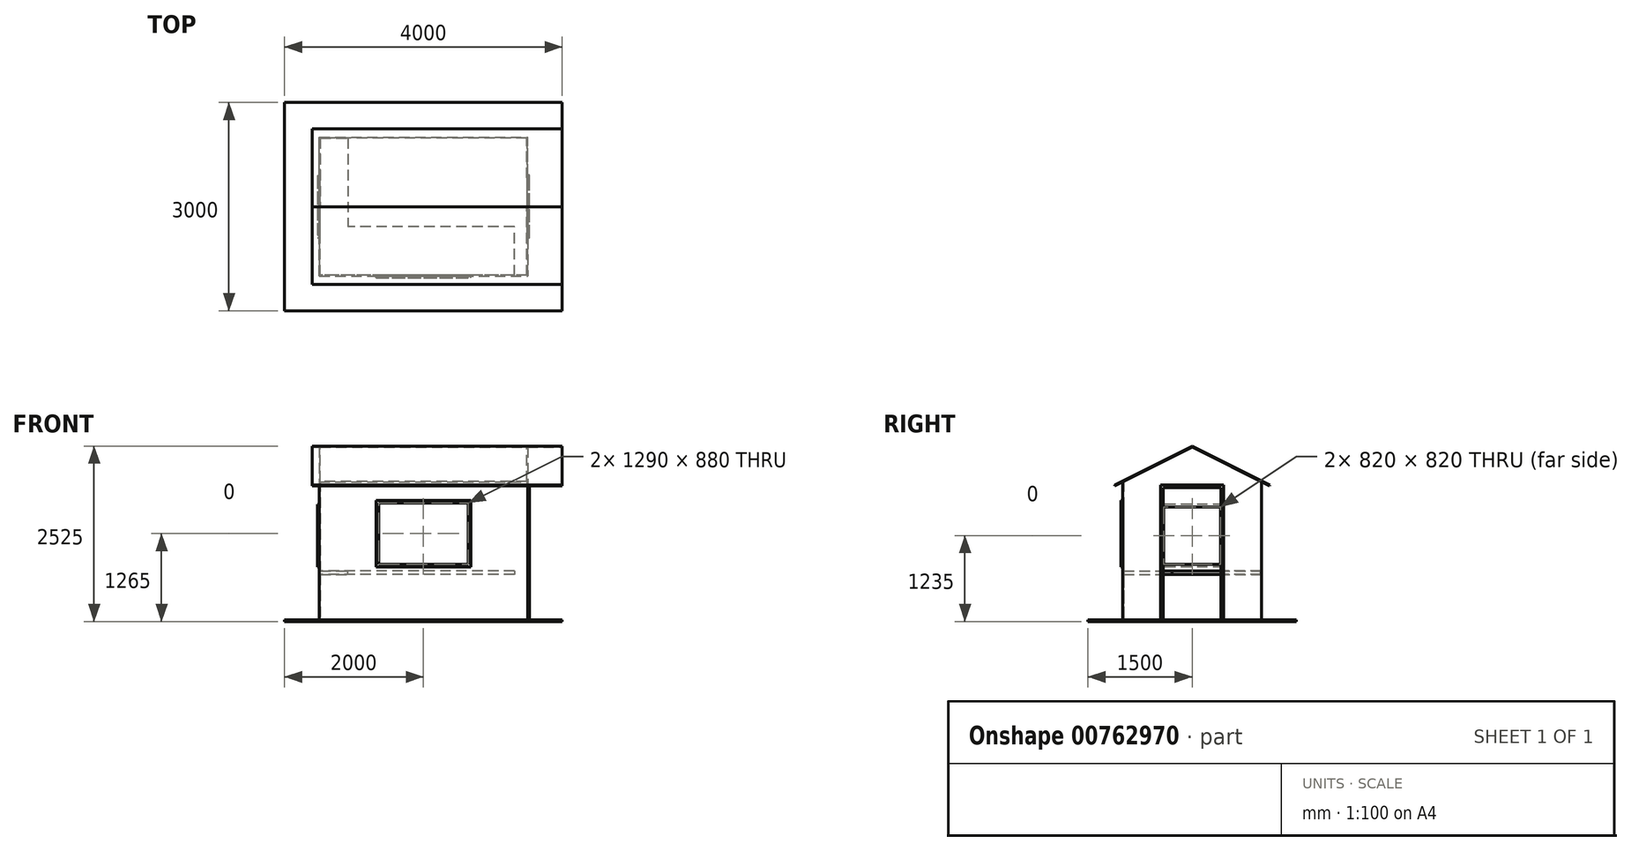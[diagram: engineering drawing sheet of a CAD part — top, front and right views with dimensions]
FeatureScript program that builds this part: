
annotation { "Feature Type Name" : "Feature", "Feature Type Description" : "" }
export const myFeature = defineFeature(function(context is Context, id is Id, definition is map)
    precondition{}
    {
        {
            var Q0;
            Q0=qCreatedBy(makeId("Top.planeOp"),FACE);
            var sketch = newSketch(context, id + "F0", { "sketchPlane" : qUnion([Q0])});
            skLineSegment(sketch, "E0.bottom", {"start": v(2000, 1500) * mm, "end": v(-2000, 1500) * mm});
            skLineSegment(sketch, "E0.top", {"start": v(2000, -1500) * mm, "end": v(-2000, -1500) * mm});
            skLineSegment(sketch, "E0.left", {"start": v(2000, 1500) * mm, "end": v(2000, -1500) * mm});
            skLineSegment(sketch, "E0.right", {"start": v(-2000, 1500) * mm, "end": v(-2000, -1500) * mm});
            skPoint(sketch, "E0.middle", {"position": v(0, 0) * mm});
            skSolve(sketch);
        }
        {
            var Q0;
            Q0 = qSketchRegion(id + "F0", true);
            extrude(context, id + "F1", {"entities" : qUnion([Q0]), "depth" : 25 * mm, "offsetDistance" : 25 * mm});
        }
        {
            var Q0;
            Q0=makeQuery(id+"F1.opExtrude","CAP_FACE",FACE,{"disambiguationData":[OSD([sQuery(id+"F0.wireOp",EDGE,"E0.bottom"),sQuery(id+"F0.wireOp",EDGE,"E0.top"),sQuery(id+"F0.wireOp",EDGE,"E0.left"),sQuery(id+"F0.wireOp",EDGE,"E0.right")])],"isStart":false});
            var sketch = newSketch(context, id + "F2", { "sketchPlane" : qUnion([Q0])});
            skLineSegment(sketch, "E1.bottom", {"start": v(1500, -1000) * mm, "end": v(-1500, -1000) * mm});
            skLineSegment(sketch, "E1.top", {"start": v(1500, 1000) * mm, "end": v(-1500, 1000) * mm});
            skLineSegment(sketch, "E1.left", {"start": v(1500, -1000) * mm, "end": v(1500, 1000) * mm});
            skLineSegment(sketch, "E1.right", {"start": v(-1500, -1000) * mm, "end": v(-1500, 1000) * mm});
            skPoint(sketch, "E1.middle", {"position": v(0, 0) * mm});
            skLineSegment(sketch, "E2.0", {"start": v(-1488, -988) * mm, "end": v(-1488, 988) * mm});
            skLineSegment(sketch, "E2.1", {"start": v(1488, -988) * mm, "end": v(-1488, -988) * mm});
            skLineSegment(sketch, "E2.2", {"start": v(1488, -988) * mm, "end": v(1488, 988) * mm});
            skLineSegment(sketch, "E2.3", {"start": v(1488, 988) * mm, "end": v(-1488, 988) * mm});
            skSolve(sketch);
        }
        {
            var Q0;
            Q0 = qSketchRegion(id + "F2", true);
            extrude(context, id + "F3", {"entities" : qUnion([Q0]), "depth" : 2500 * mm, "offsetDistance" : 25 * mm});
        }
        {
            var Q0;
            Q0=makeQuery(id+"F3.opExtrude","SWEPT_FACE",FACE,{"disambiguationData":[OSD([sQuery(id+"F2.wireOp",EDGE,"E1.right")])]});
            var sketch = newSketch(context, id + "F4", { "sketchPlane" : qUnion([Q0])});
            skLineSegment(sketch, "E3.bottom", {"start": v(-410, 1645) * mm, "end": v(410, 1645) * mm});
            skLineSegment(sketch, "E3.top", {"start": v(-410, 825) * mm, "end": v(410, 825) * mm});
            skLineSegment(sketch, "E3.left", {"start": v(-410, 1645) * mm, "end": v(-410, 825) * mm});
            skLineSegment(sketch, "E3.right", {"start": v(410, 1645) * mm, "end": v(410, 825) * mm});
            skLineSegment(sketch, "E4", {"start": v(0, 2525) * mm, "end": v(0, 25) * mm, "construction": true});
            skLineSegment(sketch, "E5.0", {"start": v(-450, 1685) * mm, "end": v(-450, 785) * mm});
            skLineSegment(sketch, "E5.1", {"start": v(-450, 1685) * mm, "end": v(450, 1685) * mm});
            skLineSegment(sketch, "E5.2", {"start": v(450, 1685) * mm, "end": v(450, 785) * mm});
            skLineSegment(sketch, "E5.3", {"start": v(-450, 785) * mm, "end": v(450, 785) * mm});
            skSolve(sketch);
        }
        {
            var Q0;
            Q0 = qSketchRegion(id + "F4", true);
            extrude(context, id + "F5", {"entities" : qUnion([Q0]), "depth" : 25 * mm, "offsetDistance" : 25 * mm});
        }
        {
            var Q0;
            Q0=makeQuery(id+"F4.imprint","IMPRINT",FACE,{"disambiguationData":[TD([[makeQuery(id+"F4.imprint","IMPRINT",EDGE,{"derivedFrom":sQuery(id+"F4.wireOp",EDGE,"E3.bottom")}),-1.0]])]});
            var Q1;
            Q1=makeQuery(id+"F3.opExtrude","SWEPT_FACE",FACE,{"disambiguationData":[OSD([sQuery(id+"F2.wireOp",EDGE,"E2.0")])]});
            extrude(context, id + "F6", {"entities" : qUnion([Q0]), "operationType" : NewBodyOperationType.REMOVE, "endBound" : BoundingType.UP_TO_SURFACE, "oppositeDirection" : true, "depth" : 25 * mm, "endBoundEntityFace" : qUnion([Q1]), "offsetDistance" : 25 * mm});
        }
        {
            var Q0;
            Q0=makeQuery(id+"F3.opExtrude","SWEPT_FACE",FACE,{"disambiguationData":[OSD([sQuery(id+"F2.wireOp",EDGE,"E1.bottom")])]});
            var sketch = newSketch(context, id + "F7", { "sketchPlane" : qUnion([Q0])});
            skLineSegment(sketch, "E6.bottom", {"start": v(-645, 825) * mm, "end": v(645, 825) * mm});
            skLineSegment(sketch, "E6.top", {"start": v(-645, 1705) * mm, "end": v(645, 1705) * mm});
            skLineSegment(sketch, "E6.left", {"start": v(-645, 825) * mm, "end": v(-645, 1705) * mm});
            skLineSegment(sketch, "E6.right", {"start": v(645, 825) * mm, "end": v(645, 1705) * mm});
            skLineSegment(sketch, "E7.0", {"start": v(-685, 1745) * mm, "end": v(685, 1745) * mm});
            skLineSegment(sketch, "E7.1", {"start": v(-685, 785) * mm, "end": v(-685, 1745) * mm});
            skLineSegment(sketch, "E7.2", {"start": v(-685, 785) * mm, "end": v(685, 785) * mm});
            skLineSegment(sketch, "E7.3", {"start": v(685, 785) * mm, "end": v(685, 1745) * mm});
            skLineSegment(sketch, "E8", {"start": v(0, 2525) * mm, "end": v(0, 25) * mm, "construction": true});
            skSolve(sketch);
        }
        {
            var Q0;
            Q0 = qSketchRegion(id + "F7", true);
            extrude(context, id + "F8", {"entities" : qUnion([Q0]), "depth" : 25 * mm, "offsetDistance" : 25 * mm});
        }
        {
            var Q0;
            Q0=makeQuery(id+"F7.imprint","IMPRINT",FACE,{"disambiguationData":[TD([[makeQuery(id+"F7.imprint","IMPRINT",EDGE,{"derivedFrom":sQuery(id+"F7.wireOp",EDGE,"E6.bottom")}),1.0]])]});
            var Q1;
            Q1=makeQuery(id+"F3.opExtrude","SWEPT_FACE",FACE,{"disambiguationData":[OSD([sQuery(id+"F2.wireOp",EDGE,"E2.1")])]});
            extrude(context, id + "F9", {"entities" : qUnion([Q0]), "operationType" : NewBodyOperationType.REMOVE, "endBound" : BoundingType.UP_TO_SURFACE, "oppositeDirection" : true, "depth" : 25 * mm, "endBoundEntityFace" : qUnion([Q1]), "offsetDistance" : 25 * mm});
        }
        {
            var Q0;
            Q0=makeQuery(id+"F3.opExtrude","SWEPT_FACE",FACE,{"disambiguationData":[OSD([sQuery(id+"F2.wireOp",EDGE,"E1.left")])]});
            var sketch = newSketch(context, id + "F10", { "sketchPlane" : qUnion([Q0])});
            skLineSegment(sketch, "E9.bottom", {"start": v(-415, 25) * mm, "end": v(415, 25) * mm});
            skLineSegment(sketch, "E9.top", {"start": v(-415, 1925) * mm, "end": v(415, 1925) * mm});
            skLineSegment(sketch, "E9.left", {"start": v(-415, 25) * mm, "end": v(-415, 1925) * mm});
            skLineSegment(sketch, "E9.right", {"start": v(415, 25) * mm, "end": v(415, 1925) * mm});
            skLineSegment(sketch, "E10", {"start": v(0, 2525) * mm, "end": v(0, 0) * mm, "construction": true});
            skLineSegment(sketch, "E11.0", {"start": v(-455, 25) * mm, "end": v(-455, 1965) * mm});
            skLineSegment(sketch, "E11.1", {"start": v(-455, 1965) * mm, "end": v(455, 1965) * mm});
            skLineSegment(sketch, "E11.2", {"start": v(455, 25) * mm, "end": v(455, 1965) * mm});
            skLineSegment(sketch, "E12", {"start": v(0, 2525) * mm, "end": v(1000, 2025) * mm});
            skLineSegment(sketch, "E13", {"start": v(0, 2525) * mm, "end": v(-1000, 2025) * mm});
            skLineSegment(sketch, "E14.0", {"start": v(0, 2511.58) * mm, "end": v(-1000, 2011.58) * mm});
            skLineSegment(sketch, "E14.1", {"start": v(0, 2511.58) * mm, "end": v(1000, 2011.58) * mm});
            skLineSegment(sketch, "E15", {"start": v(-1000, 2025) * mm, "end": v(-1118.03, 1965.98) * mm});
            skLineSegment(sketch, "E16", {"start": v(-1118.03, 1965.98) * mm, "end": v(-1112.67, 1955.25) * mm});
            skLineSegment(sketch, "E17", {"start": v(-1112.67, 1955.25) * mm, "end": v(-1000, 2011.58) * mm});
            skLineSegment(sketch, "E18.MirrorCS", {"start": v(1118.03, 1965.98) * mm, "end": v(1112.67, 1955.25) * mm});
            skLineSegment(sketch, "E19.MirrorCS", {"start": v(1000, 2025) * mm, "end": v(1118.03, 1965.98) * mm});
            skLineSegment(sketch, "E20.MirrorCS", {"start": v(1112.67, 1955.25) * mm, "end": v(1000, 2011.58) * mm});
            skSolve(sketch);
        }
        {
            var Q0;
            Q0=makeQuery(id+"F10.imprint","IMPRINT",FACE,{"disambiguationData":[TD([[makeQuery(id+"F10.imprint","IMPRINT",EDGE,{"derivedFrom":sQuery(id+"F10.wireOp",EDGE,"E9.top")}),1.0]])]});
            extrude(context, id + "F11", {"entities" : qUnion([Q0]), "depth" : 25 * mm, "offsetDistance" : 25 * mm});
        }
        {
            var Q0;
            Q0=makeQuery(id+"F10.imprint","IMPRINT",FACE,{"disambiguationData":[TD([[makeQuery(id+"F10.imprint","IMPRINT",EDGE,{"derivedFrom":sQuery(id+"F10.wireOp",EDGE,"E9.bottom")}),1.0]])]});
            extrude(context, id + "F12", {"entities" : qUnion([Q0]), "operationType" : NewBodyOperationType.REMOVE, "oppositeDirection" : true, "depth" : 25 * mm, "offsetDistance" : 25 * mm});
        }
        {
            var Q0;
            {var subQ0=sQuery(id+"F10.wireOp",EDGE,"E13");Q0=makeQuery(id+"F10.imprint","IMPRINT",FACE,{"disambiguationData":[TD([[makeQuery(id+"F10.imprint","IMPRINT",EDGE,{"derivedFrom":subQ0}),-1.0]])]});}
            var Q1;
            {var subQ0=sQuery(id+"F10.wireOp",EDGE,"E12");Q1=makeQuery(id+"F10.imprint","IMPRINT",FACE,{"disambiguationData":[TD([[makeQuery(id+"F10.imprint","IMPRINT",EDGE,{"derivedFrom":subQ0}),1.0]])]});}
            var Q2;
            {var subQ5=sQuery(id+"F10.wireOp",EDGE,"E12");Q2=makeQuery(id+"F10.imprint","IMPRINT",FACE,{"disambiguationData":[TD([[makeQuery(id+"F10.imprint","IMPRINT",EDGE,{"derivedFrom":subQ5}),-1.0]])]});}
            var Q3;
            Q3=makeQuery(id+"F3.opExtrude","SWEPT_FACE",FACE,{"disambiguationData":[OSD([sQuery(id+"F2.wireOp",EDGE,"E1.right")])]});
            extrude(context, id + "F13", {"entities" : qUnion([Q0, Q1, Q2]), "operationType" : NewBodyOperationType.REMOVE, "endBound" : BoundingType.UP_TO_SURFACE, "oppositeDirection" : true, "depth" : 25 * mm, "endBoundEntityFace" : qUnion([Q3]), "offsetDistance" : 25 * mm});
        }
        {
            var Q0;
            {var subQ5=sQuery(id+"F10.wireOp",EDGE,"E12");Q0=makeQuery(id+"F10.imprint","IMPRINT",FACE,{"disambiguationData":[TD([[makeQuery(id+"F10.imprint","IMPRINT",EDGE,{"derivedFrom":subQ5}),-1.0]])]});}
            var Q1;
            Q1=makeQuery(id+"F10.imprint","IMPRINT",FACE,{"disambiguationData":[TD([[makeQuery(id+"F10.imprint","IMPRINT",EDGE,{"derivedFrom":sQuery(id+"F10.wireOp",EDGE,"E18.MirrorCS")}),-1.0]])]});
            var Q2;
            {var subQ0=sQuery(id+"F10.wireOp",EDGE,"E15");Q2=makeQuery(id+"F10.imprint","IMPRINT",FACE,{"disambiguationData":[TD([[makeQuery(id+"F10.imprint","IMPRINT",EDGE,{"derivedFrom":subQ0}),1.0]])]});}
            extrude(context, id + "F14", {"entities" : qUnion([Q0, Q1, Q2]), "oppositeDirection" : true, "depth" : 3100 * mm, "offsetDistance" : 25 * mm});
        }
        {
            var Q0;
            {var subQ0=sQuery(id+"F10.wireOp",EDGE,"E15");Q0=makeQuery(id+"F10.imprint","IMPRINT",FACE,{"disambiguationData":[TD([[makeQuery(id+"F10.imprint","IMPRINT",EDGE,{"derivedFrom":subQ0}),1.0]])]});}
            var Q1;
            {var subQ5=sQuery(id+"F10.wireOp",EDGE,"E12");Q1=makeQuery(id+"F10.imprint","IMPRINT",FACE,{"disambiguationData":[TD([[makeQuery(id+"F10.imprint","IMPRINT",EDGE,{"derivedFrom":subQ5}),-1.0]])]});}
            var Q2;
            Q2=makeQuery(id+"F10.imprint","IMPRINT",FACE,{"disambiguationData":[TD([[makeQuery(id+"F10.imprint","IMPRINT",EDGE,{"derivedFrom":sQuery(id+"F10.wireOp",EDGE,"E18.MirrorCS")}),-1.0]])]});
            extrude(context, id + "F15", {"entities" : qUnion([Q0, Q1, Q2]), "operationType" : NewBodyOperationType.ADD, "depth" : 500 * mm, "offsetDistance" : 25 * mm});
        }
        {
            var Q0;
            Q0=makeQuery(id+"F3.opExtrude","SWEPT_FACE",FACE,{"disambiguationData":[OSD([sQuery(id+"F2.wireOp",EDGE,"E2.0")])]});
            var sketch = newSketch(context, id + "F16", { "sketchPlane" : qUnion([Q0])});
            skLineSegment(sketch, "E21.bottom", {"start": v(-988, 675) * mm, "end": v(-288, 675) * mm});
            skLineSegment(sketch, "E21.top", {"start": v(-988, 725) * mm, "end": v(-288, 725) * mm});
            skLineSegment(sketch, "E21.left", {"start": v(-988, 675) * mm, "end": v(-988, 725) * mm});
            skLineSegment(sketch, "E21.right", {"start": v(-288, 675) * mm, "end": v(-288, 725) * mm});
            skSolve(sketch);
        }
        {
            var Q0;
            Q0 = qSketchRegion(id + "F16", true);
            extrude(context, id + "F17", {"entities" : qUnion([Q0]), "depth" : 2800 * mm, "offsetDistance" : 25 * mm});
        }
        {
            var Q0;
            Q0=makeQuery(id+"F17.opExtrude","SWEPT_FACE",FACE,{"disambiguationData":[OSD([sQuery(id+"F16.wireOp",EDGE,"E21.right")])]});
            var sketch = newSketch(context, id + "F18", { "sketchPlane" : qUnion([Q0])});
            skLineSegment(sketch, "E22.0.0", {"start": v(1488, 675) * mm, "end": v(1488, 725) * mm});
            skLineSegment(sketch, "E22.0.1", {"start": v(1488, 725) * mm, "end": v(-1312, 725) * mm});
            skLineSegment(sketch, "E22.0.2", {"start": v(-1312, 725) * mm, "end": v(-1312, 675) * mm});
            skLineSegment(sketch, "E22.0.3", {"start": v(-1312, 675) * mm, "end": v(1488, 675) * mm});
            skLineSegment(sketch, "E23", {"start": v(1088, 725) * mm, "end": v(1088, 675) * mm});
            skSolve(sketch);
        }
        {
            var Q0;
            {var subQ0=sQuery(id+"F18.wireOp",EDGE,"E22.0.0");Q0=makeQuery(id+"F18.imprint","IMPRINT",FACE,{"disambiguationData":[TD([[makeQuery(id+"F18.imprint","IMPRINT",EDGE,{"derivedFrom":subQ0}),1.0]])]});}
            var Q1;
            Q1=makeQuery(id+"F3.opExtrude","SWEPT_FACE",FACE,{"disambiguationData":[OSD([sQuery(id+"F2.wireOp",EDGE,"E2.3")])]});
            extrude(context, id + "F19", {"entities" : qUnion([Q0]), "operationType" : NewBodyOperationType.ADD, "endBound" : BoundingType.UP_TO_SURFACE, "depth" : 25 * mm, "endBoundEntityFace" : qUnion([Q1]), "offsetDistance" : 25 * mm});
        }
    });
